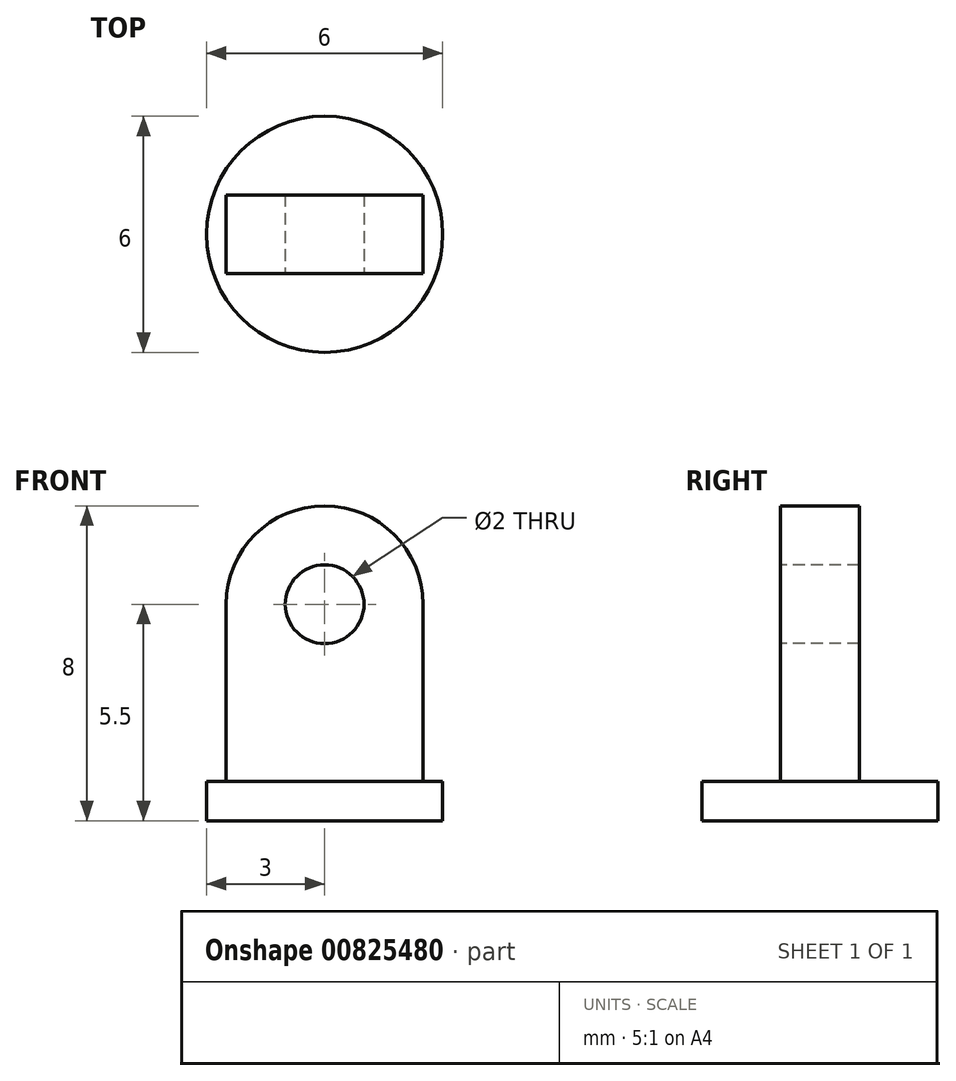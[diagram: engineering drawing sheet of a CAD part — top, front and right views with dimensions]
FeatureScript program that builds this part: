
annotation { "Feature Type Name" : "Feature", "Feature Type Description" : "" }
export const myFeature = defineFeature(function(context is Context, id is Id, definition is map)
    precondition{}
    {
        {
            var Q0;
            Q0=qCreatedBy(makeId("Top.planeOp"),FACE);
            var sketch = newSketch(context, id + "F0", { "sketchPlane" : qUnion([Q0])});
            skCircle(sketch, "E0", {"center": v(0, 0) * mm, "radius": 3 * mm});
            skSolve(sketch);
        }
        {
            var Q0;
            Q0=makeQuery(id+"F0.imprint","IMPRINT",FACE,{"disambiguationData":[TD([[makeQuery(id+"F0.imprint","IMPRINT",EDGE,{"derivedFrom":sQuery(id+"F0.wireOp",EDGE,"E0")}),1.0]])]});
            extrude(context, id + "F1", {"entities" : qUnion([Q0]), "depth" : 1 * mm, "offsetDistance" : 25 * mm});
        }
        {
            var Q0;
            Q0=makeQuery(id+"F1.opExtrude","CAP_FACE",FACE,{"disambiguationData":[OSD([sQuery(id+"F0.wireOp",EDGE,"E0")])],"isStart":false});
            var sketch = newSketch(context, id + "F2", { "sketchPlane" : qUnion([Q0])});
            skLineSegment(sketch, "E1.bottom", {"start": v(2.5, 1) * mm, "end": v(-2.5, 1) * mm});
            skLineSegment(sketch, "E1.top", {"start": v(2.5, -1) * mm, "end": v(-2.5, -1) * mm});
            skLineSegment(sketch, "E1.left", {"start": v(2.5, 1) * mm, "end": v(2.5, -1) * mm});
            skLineSegment(sketch, "E1.right", {"start": v(-2.5, 1) * mm, "end": v(-2.5, -1) * mm});
            skPoint(sketch, "E1.middle", {"position": v(0, 0) * mm});
            skSolve(sketch);
        }
        {
            var Q0;
            Q0=makeQuery(id+"F2.imprint","IMPRINT",FACE,{"disambiguationData":[TD([[makeQuery(id+"F2.imprint","IMPRINT",EDGE,{"derivedFrom":sQuery(id+"F2.wireOp",EDGE,"E1.bottom")}),1.0]])]});
            extrude(context, id + "F3", {"entities" : qUnion([Q0]), "operationType" : NewBodyOperationType.ADD, "depth" : 7 * mm, "offsetDistance" : 25 * mm});
        }
        {
            var Q0;
            Q0=makeQuery(id+"F3.opExtrude","CAP_EDGE",EDGE,{"disambiguationData":[OSD([sQuery(id+"F2.wireOp",EDGE,"E1.right")])],"isStart":false});
            var Q1;
            Q1=makeQuery(id+"F3.opExtrude","CAP_EDGE",EDGE,{"disambiguationData":[OSD([sQuery(id+"F2.wireOp",EDGE,"E1.left")])],"isStart":false});
            fillet(context, id + "F4", {"entities" : qUnion([Q0, Q1]), "radius" : 2.5 * mm, "tangentPropagation" : true, "allowEdgeOverflow" : false});
        }
        {
            var Q0;
            Q0=makeQuery(id+"F3.opExtrude","SWEPT_FACE",FACE,{"disambiguationData":[OSD([sQuery(id+"F2.wireOp",EDGE,"E1.top")])]});
            var sketch = newSketch(context, id + "F5", { "sketchPlane" : qUnion([Q0])});
            skCircle(sketch, "E2", {"center": v(0, 5.5) * mm, "radius": 1 * mm});
            skSolve(sketch);
        }
        {
            var Q0;
            Q0=makeQuery(id+"F5.imprint","IMPRINT",FACE,{"disambiguationData":[TD([[makeQuery(id+"F5.imprint","IMPRINT",EDGE,{"derivedFrom":sQuery(id+"F5.wireOp",EDGE,"E2")}),1.0]])]});
            extrude(context, id + "F6", {"entities" : qUnion([Q0]), "operationType" : NewBodyOperationType.REMOVE, "oppositeDirection" : true, "depth" : 4 * mm, "offsetDistance" : 25 * mm});
        }
    });
